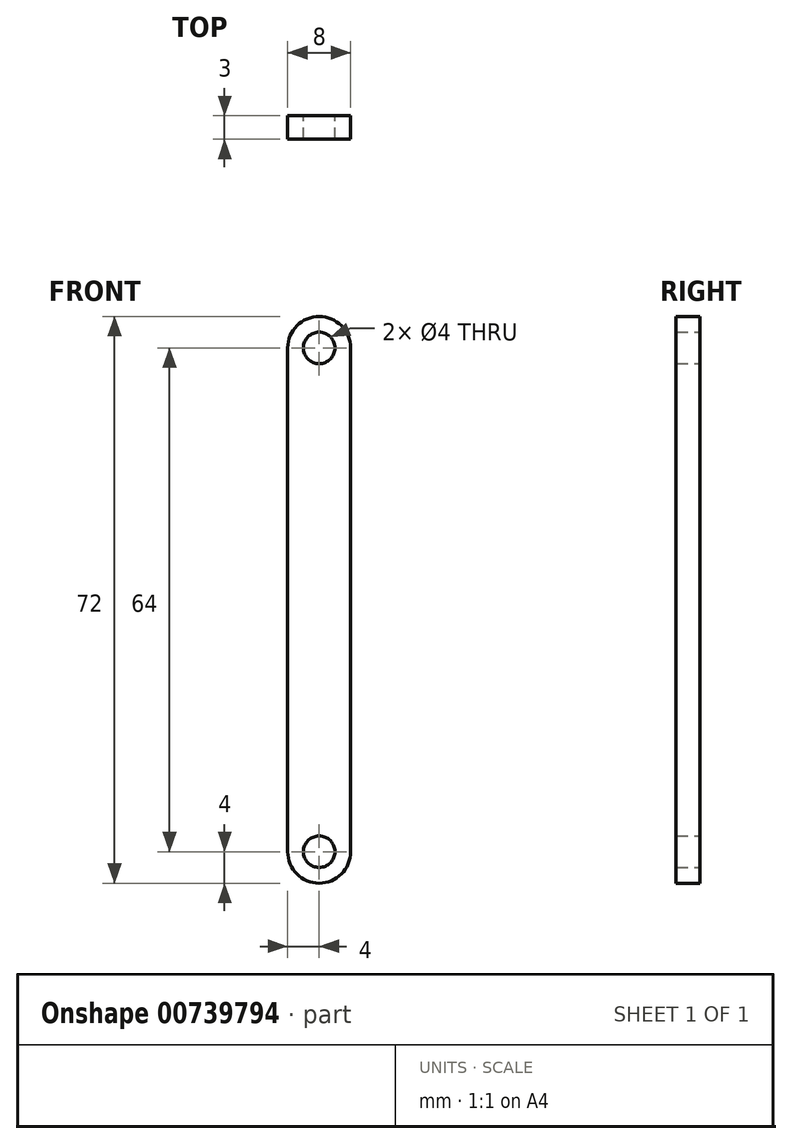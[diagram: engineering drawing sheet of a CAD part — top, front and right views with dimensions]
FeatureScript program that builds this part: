
annotation { "Feature Type Name" : "Feature", "Feature Type Description" : "" }
export const myFeature = defineFeature(function(context is Context, id is Id, definition is map)
    precondition{}
    {
        {
            var Q0;
            Q0=qCreatedBy(makeId("Front.planeOp"),FACE);
            var sketch = newSketch(context, id + "F0", { "sketchPlane" : qUnion([Q0])});
            skLineSegment(sketch, "E0.bottom", {"start": v(4, 32) * mm, "end": v(-4, 32) * mm, "construction": true});
            skLineSegment(sketch, "E0.top", {"start": v(4, -32) * mm, "end": v(-4, -32) * mm, "construction": true});
            skLineSegment(sketch, "E0.left", {"start": v(4, 32) * mm, "end": v(4, -32) * mm});
            skLineSegment(sketch, "E0.right", {"start": v(-4, 32) * mm, "end": v(-4, -32) * mm});
            skPoint(sketch, "E0.middle", {"position": v(0, 0) * mm});
            skArc(sketch, "E1", {"start": v(-4, -32) * mm, "mid": v(0, -36) * mm, "end": v(4, -32) * mm});
            skArc(sketch, "E2", {"start": v(4, 32) * mm, "mid": v(0, 36) * mm, "end": v(-4, 32) * mm});
            skCircle(sketch, "E3", {"center": v(0, 32) * mm, "radius": 2 * mm});
            skCircle(sketch, "E4", {"center": v(0, -32) * mm, "radius": 2 * mm});
            skSolve(sketch);
        }
        {
            var Q0;
            Q0 = qSketchRegion(id + "F0", true);
            extrude(context, id + "F1", {"entities" : qUnion([Q0]), "depth" : 3 * mm, "offsetDistance" : 25 * mm});
        }
    });
